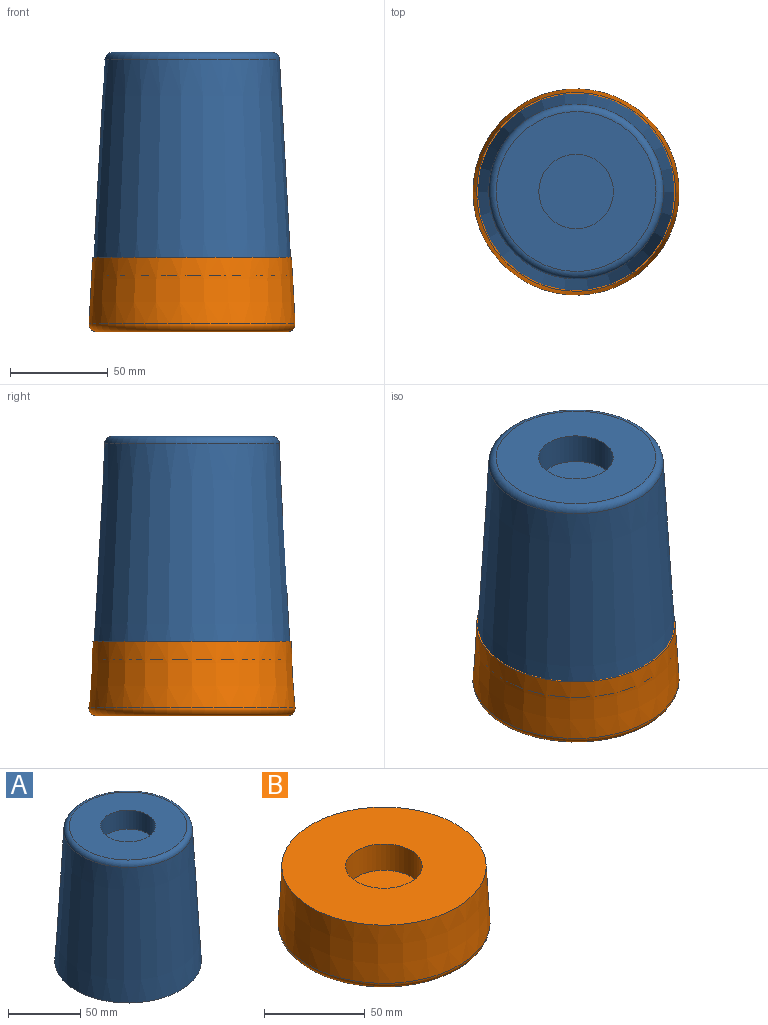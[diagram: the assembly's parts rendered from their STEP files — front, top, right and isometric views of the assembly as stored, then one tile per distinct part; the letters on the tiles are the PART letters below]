
ASSEMBLY  parts=2 mates=1
PART A: 8 faces, bbox 101.6x101.6x120.7 mm
  f0: plane 81.69x81.69mm, normal (0,0,1), area 4101.3mm2, adj f1,f6
  f1: torus R=40.85mm, axis (0,0,1), area 1567.8mm2, adj f0,f2
  f2: cone r=50.8mm half-angle=3.2deg, axis (0,0,-1), area 33246.6mm2, adj f1,f3
  f3: plane 101.6x101.6mm, normal (0,0,-1), area 6967.2mm2, adj f2,f4
  f4: cylinder r=19.05mm len=38.1mm, axis (0,0,1), area 760.1mm2, adj f3,f5
  f5: plane 38.1x38.1mm, normal (0,0,-1), area 1140.1mm2, adj f4
  f6: cylinder r=19.05mm len=38.1mm, axis (0,0,1), area 1915.4mm2, adj f0,f7
  f7: plane 38.1x38.1mm, normal (0,0,1), area 1140.1mm2, adj f6
PART B: 6 faces, bbox 114.1x114.1x38.1 mm
  f0: torus R=48.89mm, axis (0,0,-1), area 1999.6mm2, adj f1,f3
  f1: plane 97.78x97.78mm, normal (0,0,-1), area 7508.9mm2, adj f0
  f2: plane 101.6x101.6mm, normal (0,0,1), area 6967.2mm2, adj f3,f4
  f3: cone r=50.8mm half-angle=3.2deg, axis (0,0,-1), area 11097.2mm2, adj f0,f2
  f4: cylinder r=19.05mm len=38.1mm, axis (0,0,1), area 1915.4mm2, adj f2,f5
  f5: plane 38.1x38.1mm, normal (0,0,1), area 1140.1mm2, adj f4
PLACE A t=(-113.19,-108.59,-13.35)mm
PLACE B t=(-113.19,-108.59,-70.8)mm
MATE fastened A.f1 <-> B.f0  axis (0,0,-1) through (-113.19,-108.59,-73.03)mm
